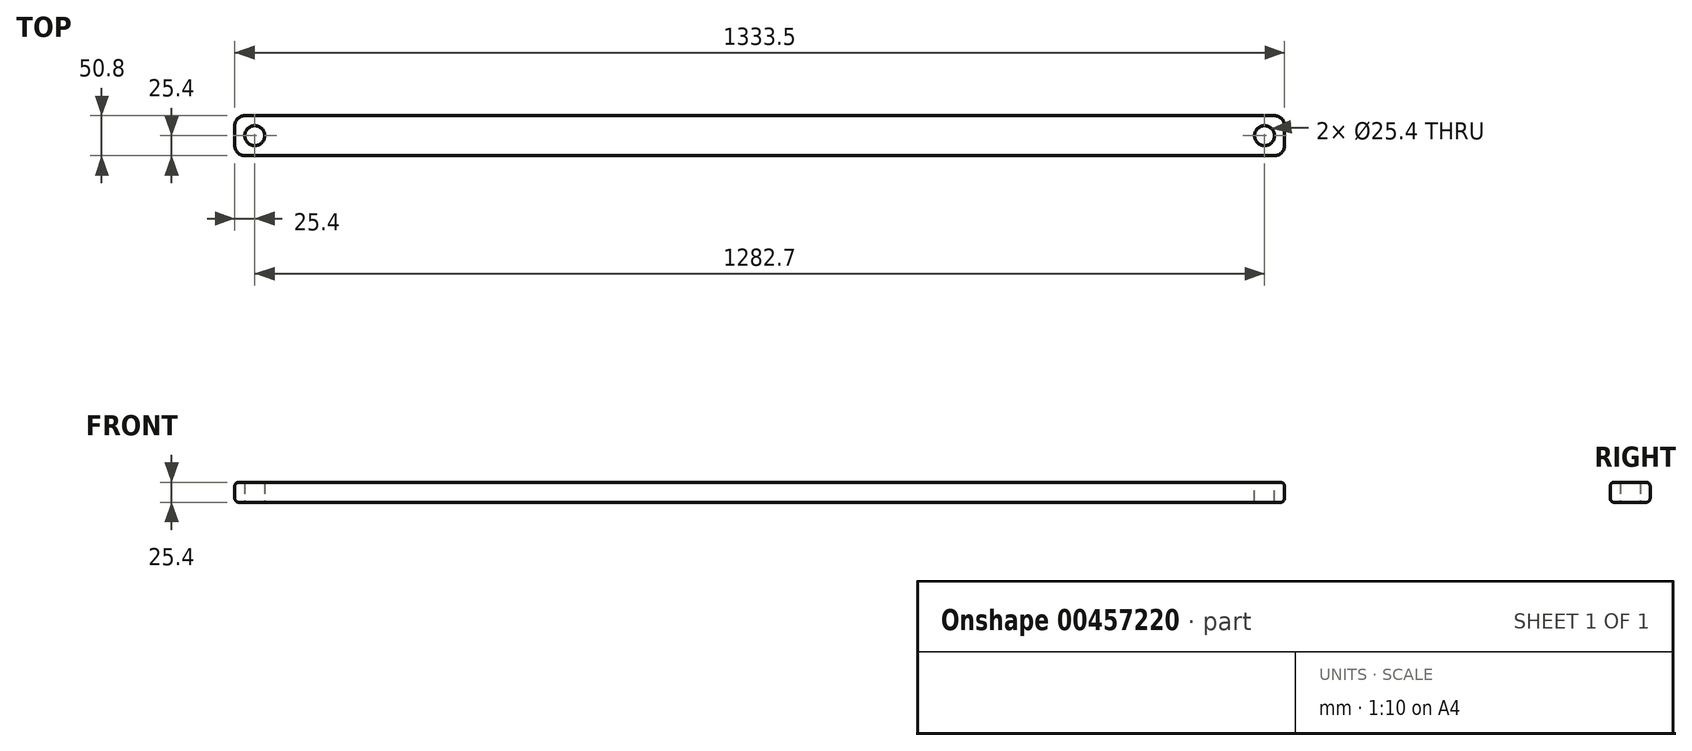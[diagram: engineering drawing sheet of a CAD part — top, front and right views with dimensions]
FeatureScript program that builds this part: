
annotation { "Feature Type Name" : "Feature", "Feature Type Description" : "" }
export const myFeature = defineFeature(function(context is Context, id is Id, definition is map)
    precondition{}
    {
        {
            var Q0;
            Q0=qCreatedBy(makeId("Top.planeOp"),FACE);
            var sketch = newSketch(context, id + "F0", { "sketchPlane" : qUnion([Q0])});
            skLineSegment(sketch, "E0.bottom", {"start": v(-538.58, 50.8) * mm, "end": v(769.52, 50.8) * mm});
            skLineSegment(sketch, "E0.top", {"start": v(-538.58, 0) * mm, "end": v(769.52, 0) * mm});
            skLineSegment(sketch, "E0.left", {"start": v(-551.28, 38.1) * mm, "end": v(-551.28, 12.7) * mm});
            skLineSegment(sketch, "E0.right", {"start": v(782.22, 38.1) * mm, "end": v(782.22, 12.7) * mm});
            skCircle(sketch, "E1", {"center": v(-525.88, 25.4) * mm, "radius": 12.7 * mm});
            skPoint(sketch, "E2.visualSharp", {"position": v(-551.28, 0) * mm});
            skArc(sketch, "E2.filletArc", {"start": v(-551.28, 12.7) * mm, "mid": v(-547.56, 3.72) * mm, "end": v(-538.58, 0) * mm});
            skPoint(sketch, "E3.visualSharp", {"position": v(-551.28, 50.8) * mm});
            skArc(sketch, "E3.filletArc", {"start": v(-538.58, 50.8) * mm, "mid": v(-547.56, 47.08) * mm, "end": v(-551.28, 38.1) * mm});
            skPoint(sketch, "E4.visualSharp", {"position": v(782.22, 50.8) * mm});
            skArc(sketch, "E4.filletArc", {"start": v(782.22, 38.1) * mm, "mid": v(778.5, 47.08) * mm, "end": v(769.52, 50.8) * mm});
            skPoint(sketch, "E5.visualSharp", {"position": v(782.22, 0) * mm});
            skArc(sketch, "E5.filletArc", {"start": v(769.52, 0) * mm, "mid": v(778.5, 3.72) * mm, "end": v(782.22, 12.7) * mm});
            skSolve(sketch);
        }
        {
            var Q0;
            Q0=makeQuery(id+"F0.imprint","IMPRINT",FACE,{"disambiguationData":[TD([[makeQuery(id+"F0.imprint","IMPRINT",EDGE,{"derivedFrom":sQuery(id+"F0.wireOp",EDGE,"E0.bottom")}),-1.0]])]});
            extrude(context, id + "F1", {"entities" : qUnion([Q0]), "depth" : 25.4 * mm});
        }
        {
            var Q0;
            Q0=makeQuery(id+"F1.opExtrude","CAP_FACE",FACE,{"disambiguationData":[OSD([sQuery(id+"F0.wireOp",EDGE,"E0.bottom"),sQuery(id+"F0.wireOp",EDGE,"E0.top"),sQuery(id+"F0.wireOp",EDGE,"E0.left"),sQuery(id+"F0.wireOp",EDGE,"E0.right"),sQuery(id+"F0.wireOp",EDGE,"E1")])],"isStart":true});
            var sketch = newSketch(context, id + "F2", { "sketchPlane" : qUnion([Q0])});
            skCircle(sketch, "E6", {"center": v(756.82, -25.4) * mm, "radius": 12.7 * mm});
            skPoint(sketch, "E6.centerSnap0", {"position": v(782.22, -25.4) * mm});
            skSolve(sketch);
        }
        {
            var Q0;
            Q0=sQuery(id+"F2.wireOp",VERTEX,"E6.center");
            var Q1;
            Q1=makeQuery(id+"F1.opExtrude","SWEPT_BODY",BODY,{"disambiguationData":[OSD([sQuery(id+"F0.wireOp",EDGE,"E0.bottom"),sQuery(id+"F0.wireOp",EDGE,"E0.top"),sQuery(id+"F0.wireOp",EDGE,"E0.left"),sQuery(id+"F0.wireOp",EDGE,"E0.right"),sQuery(id+"F0.wireOp",EDGE,"E1")])]});
            hole(context, id + "F3", {"style" : HoleStyle.SIMPLE, "endStyle" : HoleEndStyle.THROUGH, "holeDiameter" : 25.4 * mm, "isTappedThrough" : true, "tappedDepth" : 12.7 * mm, "tapClearance" : 3, "locations" : qUnion([Q0]), "scope" : qUnion([Q1]), "startStyle" : HoleStartStyle.PART});
        }
        {
            var Q0;
            Q0=makeQuery(id+"F1.opExtrude","CAP_EDGE",EDGE,{"disambiguationData":[OSD([sQuery(id+"F0.wireOp",EDGE,"E0.top")])],"isStart":true});
            var Q1;
            Q1=makeQuery(id+"F1.opExtrude","CAP_EDGE",EDGE,{"disambiguationData":[OSD([sQuery(id+"F0.wireOp",EDGE,"E0.left")])],"isStart":true});
            var Q2;
            Q2=makeQuery(id+"F1.opExtrude","CAP_EDGE",EDGE,{"disambiguationData":[OSD([sQuery(id+"F0.wireOp",EDGE,"E0.bottom")])],"isStart":true});
            var Q3;
            Q3=makeQuery(id+"F1.opExtrude","CAP_EDGE",EDGE,{"disambiguationData":[OSD([sQuery(id+"F0.wireOp",EDGE,"E0.right")])],"isStart":true});
            var Q4;
            Q4=makeQuery(id+"F1.opExtrude","CAP_EDGE",EDGE,{"disambiguationData":[OSD([sQuery(id+"F0.wireOp",EDGE,"E0.top")])],"isStart":false});
            var Q5;
            Q5=makeQuery(id+"F1.opExtrude","CAP_EDGE",EDGE,{"disambiguationData":[OSD([sQuery(id+"F0.wireOp",EDGE,"E0.right")])],"isStart":false});
            var Q6;
            Q6=makeQuery(id+"F1.opExtrude","CAP_EDGE",EDGE,{"disambiguationData":[OSD([sQuery(id+"F0.wireOp",EDGE,"E0.bottom")])],"isStart":false});
            var Q7;
            Q7=makeQuery(id+"F1.opExtrude","CAP_EDGE",EDGE,{"disambiguationData":[OSD([sQuery(id+"F0.wireOp",EDGE,"E0.left")])],"isStart":false});
            fillet(context, id + "F4", {"entities" : qUnion([Q0, Q1, Q2, Q3, Q4, Q5, Q6, Q7]), "radius" : 5.08 * mm, "tangentPropagation" : true, "allowEdgeOverflow" : false});
        }
    });
